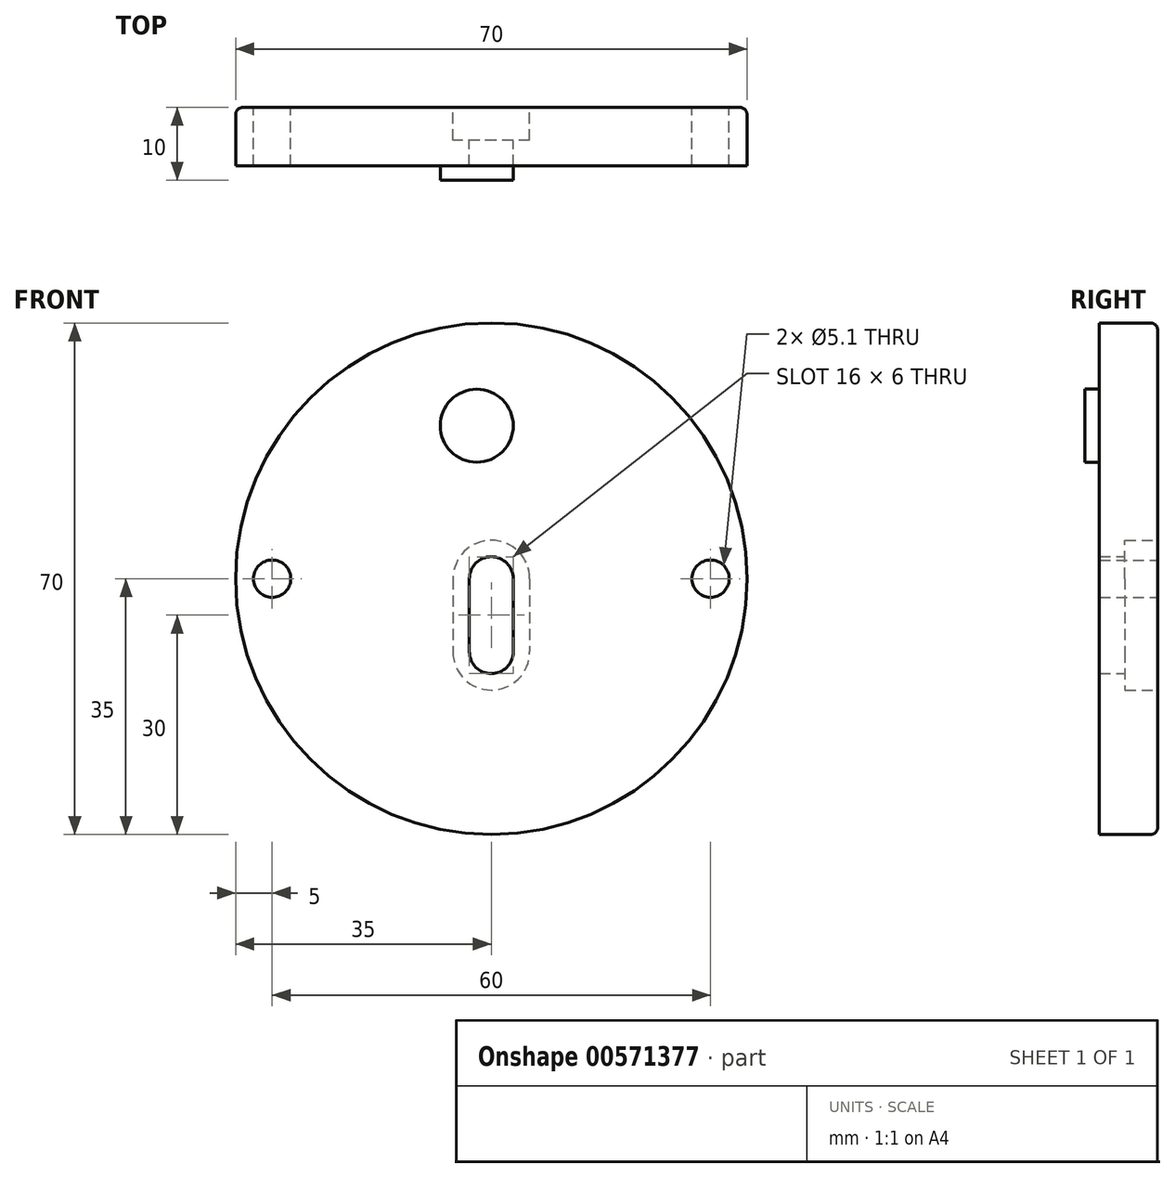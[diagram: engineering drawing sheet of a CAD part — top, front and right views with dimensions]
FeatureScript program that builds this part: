
annotation { "Feature Type Name" : "Feature", "Feature Type Description" : "" }
export const myFeature = defineFeature(function(context is Context, id is Id, definition is map)
    precondition{}
    {
        {
            var Q0;
            Q0=qCreatedBy(makeId("Front.planeOp"),FACE);
            var sketch = newSketch(context, id + "F0", { "sketchPlane" : qUnion([Q0])});
            skCircle(sketch, "E0", {"center": v(0, 0) * mm, "radius": 35 * mm});
            skArc(sketch, "E1", {"start": v(3, 0) * mm, "mid": v(0, 3) * mm, "end": v(-3, 0) * mm});
            skArc(sketch, "E2", {"start": v(5.25, 0) * mm, "mid": v(0, 5.25) * mm, "end": v(-5.25, 0) * mm});
            skCircle(sketch, "E3", {"center": v(-30, 0) * mm, "radius": 2.55 * mm});
            skCircle(sketch, "E4", {"center": v(30, 0) * mm, "radius": 2.55 * mm});
            skArc(sketch, "E5", {"start": v(-3, -10) * mm, "mid": v(0, -13) * mm, "end": v(3, -10) * mm});
            skArc(sketch, "E6", {"start": v(-5.25, -10) * mm, "mid": v(0, -15.25) * mm, "end": v(5.25, -10) * mm});
            skLineSegment(sketch, "E7", {"start": v(5.25, 0) * mm, "end": v(5.25, -10) * mm});
            skLineSegment(sketch, "E8", {"start": v(-5.25, 0) * mm, "end": v(-5.25, -10) * mm});
            skLineSegment(sketch, "E9", {"start": v(-3, 0) * mm, "end": v(-3, -10) * mm});
            skLineSegment(sketch, "E10", {"start": v(3, 0) * mm, "end": v(3, -10) * mm});
            skCircle(sketch, "E11", {"center": v(-2, 20.93) * mm, "radius": 5 * mm});
            skSolve(sketch);
        }
        {
            var Q0;
            Q0=makeQuery(id+"F0.imprint","IMPRINT",FACE,{"disambiguationData":[TD([[makeQuery(id+"F0.imprint","IMPRINT",EDGE,{"derivedFrom":sQuery(id+"F0.wireOp",EDGE,"E0")}),1.0]])]});
            extrude(context, id + "F1", {"entities" : qUnion([Q0]), "depth" : 8 * mm, "offsetDistance" : 25 * mm});
        }
        {
            var Q0;
            Q0=makeQuery(id+"F0.imprint","IMPRINT",FACE,{"disambiguationData":[TD([[makeQuery(id+"F0.imprint","IMPRINT",EDGE,{"derivedFrom":sQuery(id+"F0.wireOp",EDGE,"E1")}),-1.0]])]});
            extrude(context, id + "F2", {"entities" : qUnion([Q0]), "operationType" : NewBodyOperationType.ADD, "depth" : 8 * mm, "offsetDistance" : 25 * mm});
        }
        {
            var Q0;
            Q0=makeQuery(id+"F0.imprint","IMPRINT",FACE,{"disambiguationData":[TD([[makeQuery(id+"F0.imprint","IMPRINT",EDGE,{"derivedFrom":sQuery(id+"F0.wireOp",EDGE,"E1")}),-1.0]])]});
            extrude(context, id + "F3", {"entities" : qUnion([Q0]), "operationType" : NewBodyOperationType.REMOVE, "depth" : 4.5 * mm, "offsetDistance" : 25 * mm});
        }
        {
            var Q0;
            Q0=makeQuery(id+"F1.opExtrude","CAP_EDGE",EDGE,{"disambiguationData":[OSD([sQuery(id+"F0.wireOp",EDGE,"E0")])],"isStart":true});
            fillet(context, id + "F4", {"entities" : qUnion([Q0]), "radius" : 1 * mm, "tangentPropagation" : true, "allowEdgeOverflow" : false});
        }
        {
            var Q0;
            Q0=makeQuery(id+"F0.imprint","IMPRINT",FACE,{"disambiguationData":[TD([[makeQuery(id+"F0.imprint","IMPRINT",EDGE,{"derivedFrom":sQuery(id+"F0.wireOp",EDGE,"E11")}),1.0]])]});
            extrude(context, id + "F5", {"entities" : qUnion([Q0]), "operationType" : NewBodyOperationType.ADD, "depth" : 10 * mm, "offsetDistance" : 25 * mm});
        }
    });
